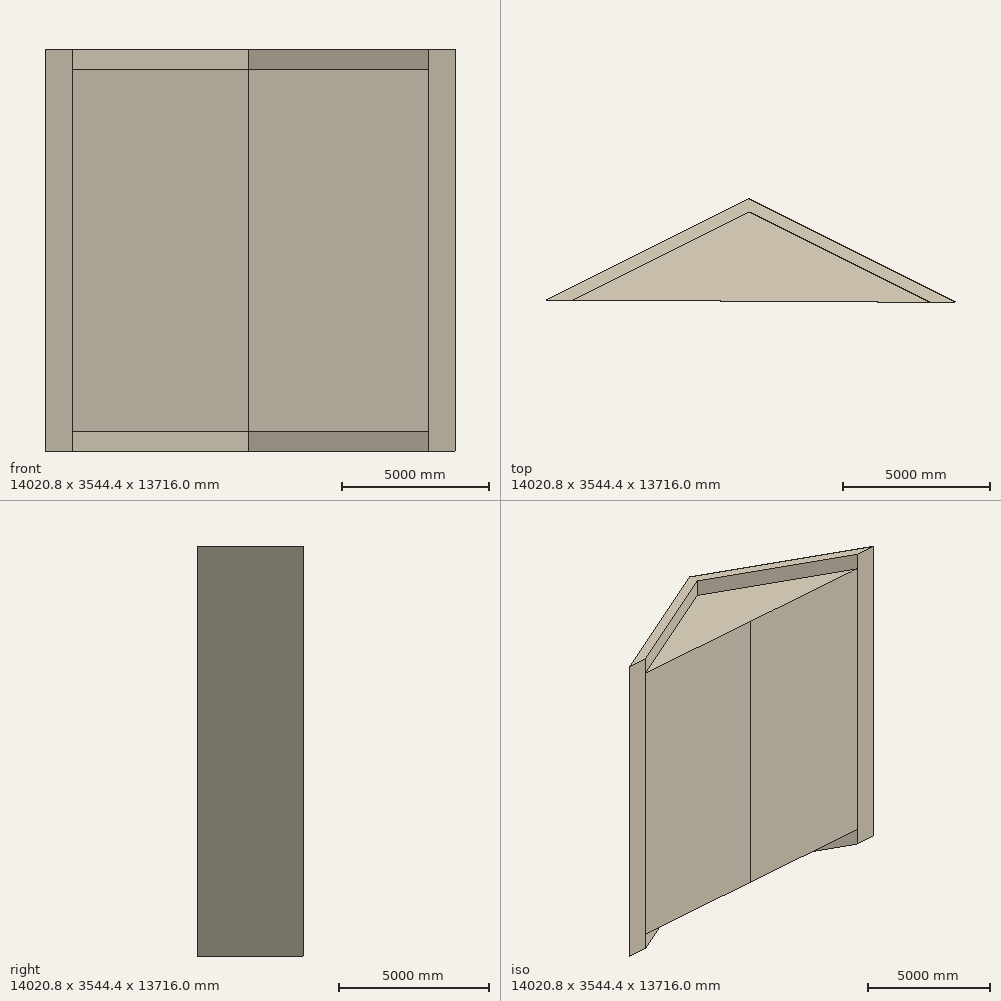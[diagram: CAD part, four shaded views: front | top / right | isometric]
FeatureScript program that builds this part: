
annotation { "Feature Type Name" : "Feature", "Feature Type Description" : "" }
export const myFeature = defineFeature(function(context is Context, id is Id, definition is map)
    precondition{}
    {
        {
            var Q0;
            Q0=qCreatedBy(makeId("Top.planeOp"),FACE);
            var sketch = newSketch(context, id + "F0", { "sketchPlane" : qUnion([Q0])});
            skLineSegment(sketch, "E0", {"start": v(6310.58, 214.72) * mm, "end": v(6310.58, 3262.72) * mm, "construction": true});
            skLineSegment(sketch, "E1", {"start": v(6310.58, 3262.72) * mm, "end": v(293.08, 253.97) * mm});
            skLineSegment(sketch, "E2", {"start": v(6310.58, 3262.72) * mm, "end": v(12485.08, 175.47) * mm});
            skLineSegment(sketch, "E3", {"start": v(6310.58, 3262.72) * mm, "end": v(6310.58, 3719.92) * mm});
            skLineSegment(sketch, "E4", {"start": v(293.08, 253.97) * mm, "end": v(-621.32, 253.97) * mm});
            skLineSegment(sketch, "E5", {"start": v(12485.08, 175.47) * mm, "end": v(13399.48, 175.47) * mm});
            skLineSegment(sketch, "E6", {"start": v(6310.58, 3719.92) * mm, "end": v(13399.48, 175.47) * mm});
            skLineSegment(sketch, "E7", {"start": v(-621.32, 253.97) * mm, "end": v(6310.58, 3719.92) * mm});
            skLineSegment(sketch, "E8", {"start": v(293.08, 253.97) * mm, "end": v(293.08, -7061.23) * mm});
            skLineSegment(sketch, "E9", {"start": v(12485.08, -7101.09) * mm, "end": v(12485.08, 175.47) * mm});
            skLineSegment(sketch, "E10", {"start": v(5881.08, -7100.48) * mm, "end": v(5931.88, -4967.49) * mm});
            skLineSegment(sketch, "E11", {"start": v(5931.88, -4967.49) * mm, "end": v(6846.28, -4967.49) * mm});
            skLineSegment(sketch, "E12", {"start": v(6846.28, -4967.49) * mm, "end": v(6846.28, -7101.09) * mm});
            skLineSegment(sketch, "E13", {"start": v(6310.58, 214.72) * mm, "end": v(6338.28, -7100.48) * mm, "construction": true});
            skLineSegment(sketch, "E14", {"start": v(293.08, -7061.23) * mm, "end": v(5881.08, -7100.48) * mm});
            skLineSegment(sketch, "E15", {"start": v(5881.08, -7100.48) * mm, "end": v(6338.28, -7100.48) * mm});
            skLineSegment(sketch, "E16", {"start": v(6338.28, -7100.48) * mm, "end": v(6846.28, -7101.09) * mm});
            skLineSegment(sketch, "E17", {"start": v(12485.08, -7101.09) * mm, "end": v(6846.28, -7101.09) * mm});
            skLineSegment(sketch, "E18.top", {"start": v(8827.48, -6186.69) * mm, "end": v(10961.08, -6186.69) * mm});
            skLineSegment(sketch, "E18.left", {"start": v(8827.48, -5272.29) * mm, "end": v(8827.48, -6186.69) * mm});
            skLineSegment(sketch, "E18.right", {"start": v(10961.08, -5272.29) * mm, "end": v(10961.08, -6186.69) * mm});
            skLineSegment(sketch, "E19.0", {"start": v(11265.88, -4967.49) * mm, "end": v(11265.88, -6491.49) * mm});
            skLineSegment(sketch, "E19.2", {"start": v(8522.68, -4967.49) * mm, "end": v(8522.68, -6491.49) * mm});
            skLineSegment(sketch, "E19.3", {"start": v(8522.68, -6491.49) * mm, "end": v(11265.88, -6491.49) * mm});
            skLineSegment(sketch, "E20", {"start": v(293.08, -7061.23) * mm, "end": v(293.08, -7366.03) * mm});
            skLineSegment(sketch, "E21", {"start": v(293.08, -7366.03) * mm, "end": v(12485.08, -7366.03) * mm});
            skLineSegment(sketch, "E22", {"start": v(12485.08, -7366.03) * mm, "end": v(12485.08, -7101.09) * mm});
            skLineSegment(sketch, "E23", {"start": v(293.08, 253.97) * mm, "end": v(6310.58, 214.72) * mm});
            skLineSegment(sketch, "E24", {"start": v(6310.58, 214.72) * mm, "end": v(12485.08, 175.47) * mm});
            skArc(sketch, "E25", {"start": v(11265.88, -4967.49) * mm, "mid": v(9894.28, -3595.89) * mm, "end": v(8522.68, -4967.49) * mm});
            skArc(sketch, "E26", {"start": v(10961.08, -5272.29) * mm, "mid": v(9894.28, -4104.03) * mm, "end": v(8827.48, -5272.29) * mm});
            skSolve(sketch);
        }
        {
            var Q0;
            Q0=makeQuery(id+"F0.imprint","IMPRINT",FACE,{"disambiguationData":[TD([[makeQuery(id+"F0.imprint","IMPRINT",EDGE,{"derivedFrom":sQuery(id+"F0.wireOp",EDGE,"E1")}),-1.0]])]});
            var Q1;
            Q1=makeQuery(id+"F0.imprint","IMPRINT",FACE,{"disambiguationData":[TD([[makeQuery(id+"F0.imprint","IMPRINT",EDGE,{"derivedFrom":sQuery(id+"F0.wireOp",EDGE,"E2")}),1.0]])]});
            extrude(context, id + "F1", {"entities" : qUnion([Q0, Q1]), "endBound" : BoundingType.SYMMETRIC, "depth" : 13716 * mm, "offsetDistance" : 30.48 * mm});
        }
        {
            var Q0;
            Q0=makeQuery(id+"F0.imprint","IMPRINT",FACE,{"disambiguationData":[TD([[makeQuery(id+"F0.imprint","IMPRINT",EDGE,{"derivedFrom":sQuery(id+"F0.wireOp",EDGE,"E1")}),1.0]])]});
            extrude(context, id + "F2", {"entities" : qUnion([Q0]), "endBound" : BoundingType.SYMMETRIC, "depth" : 12344.4 * mm, "offsetDistance" : 30.48 * mm});
        }
    });
